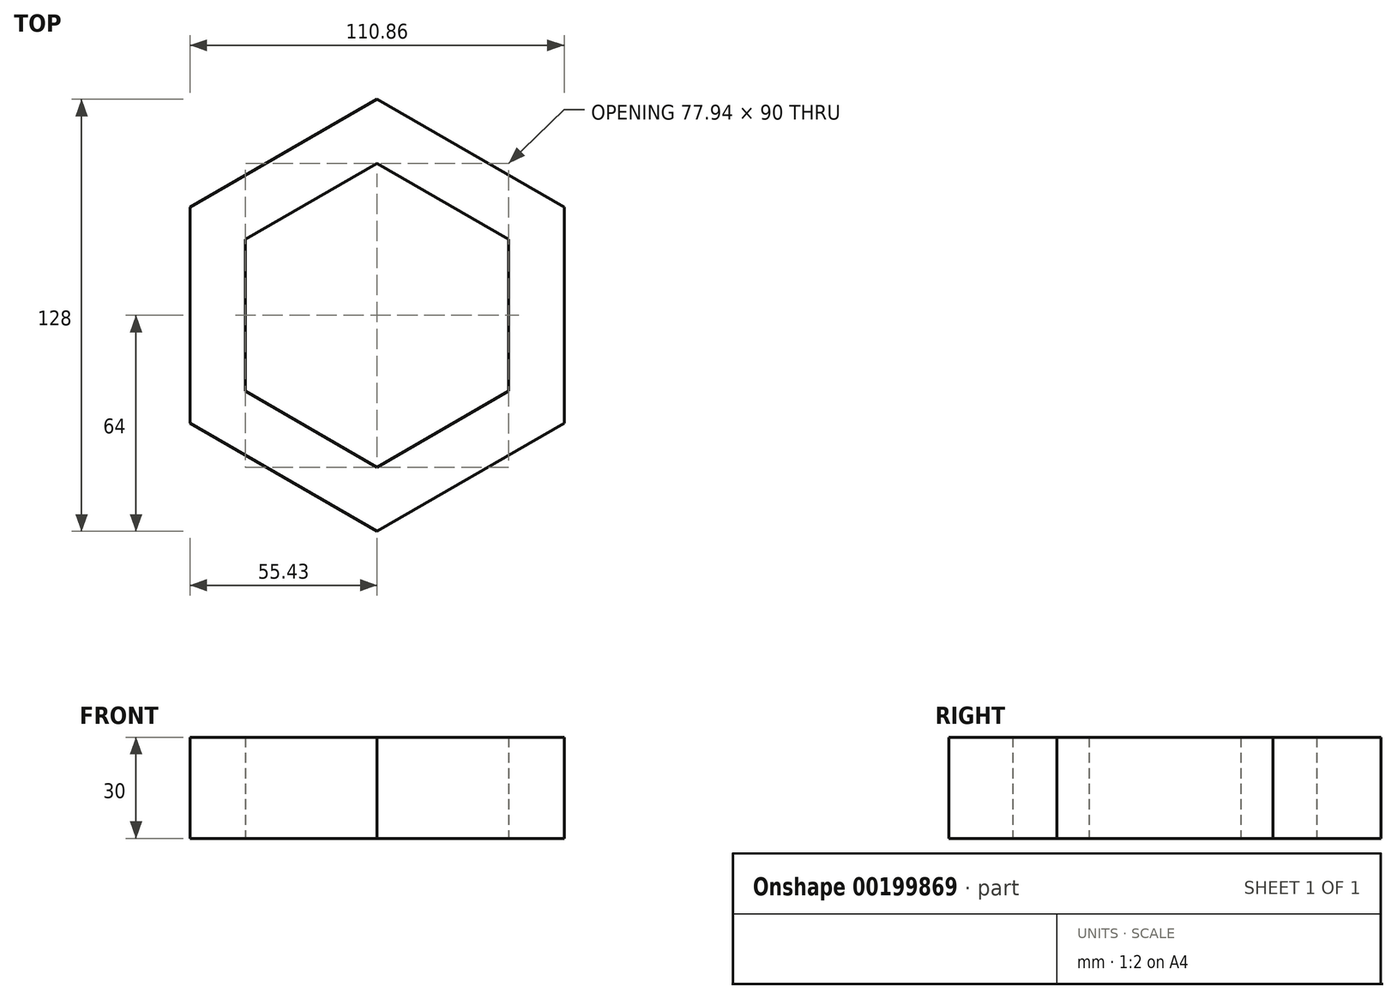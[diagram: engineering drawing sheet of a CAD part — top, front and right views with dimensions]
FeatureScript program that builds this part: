
annotation { "Feature Type Name" : "Feature", "Feature Type Description" : "" }
export const myFeature = defineFeature(function(context is Context, id is Id, definition is map)
    precondition{}
    {
        {
            var Q0;
            Q0=qCreatedBy(makeId("Top.planeOp"),FACE);
            var sketch = newSketch(context, id + "F0", { "sketchPlane" : qUnion([Q0])});
            skLineSegment(sketch, "E0", {"start": v(-38.97, 22.5) * mm, "end": v(-38.97, -22.5) * mm});
            skLineSegment(sketch, "E1", {"start": v(-38.97, -22.5) * mm, "end": v(0, -45) * mm});
            skLineSegment(sketch, "E2", {"start": v(0, -45) * mm, "end": v(38.97, -22.5) * mm});
            skLineSegment(sketch, "E3", {"start": v(38.97, -22.5) * mm, "end": v(38.97, 22.5) * mm});
            skLineSegment(sketch, "E4", {"start": v(38.97, 22.5) * mm, "end": v(0, 45) * mm});
            skLineSegment(sketch, "E5", {"start": v(0, 45) * mm, "end": v(-38.97, 22.5) * mm});
            skLineSegment(sketch, "E6", {"start": v(-55.43, 32) * mm, "end": v(0, 64) * mm});
            skLineSegment(sketch, "E7", {"start": v(0, 64) * mm, "end": v(55.43, 32) * mm});
            skLineSegment(sketch, "E8", {"start": v(55.43, 32) * mm, "end": v(55.43, -32) * mm});
            skLineSegment(sketch, "E9", {"start": v(55.43, -32) * mm, "end": v(0, -64) * mm});
            skLineSegment(sketch, "E10", {"start": v(0, -64) * mm, "end": v(-55.43, -32) * mm});
            skLineSegment(sketch, "E11", {"start": v(-55.43, -32) * mm, "end": v(-55.43, 32) * mm});
            skSolve(sketch);
        }
        {
            var Q0;
            Q0=makeQuery(id+"F0.imprint","IMPRINT",FACE,{"disambiguationData":[TD([[makeQuery(id+"F0.imprint","IMPRINT",EDGE,{"derivedFrom":sQuery(id+"F0.wireOp",EDGE,"E0")}),-1.0]])]});
            extrude(context, id + "F1", {"entities" : qUnion([Q0]), "depth" : 30 * mm});
        }
    });
